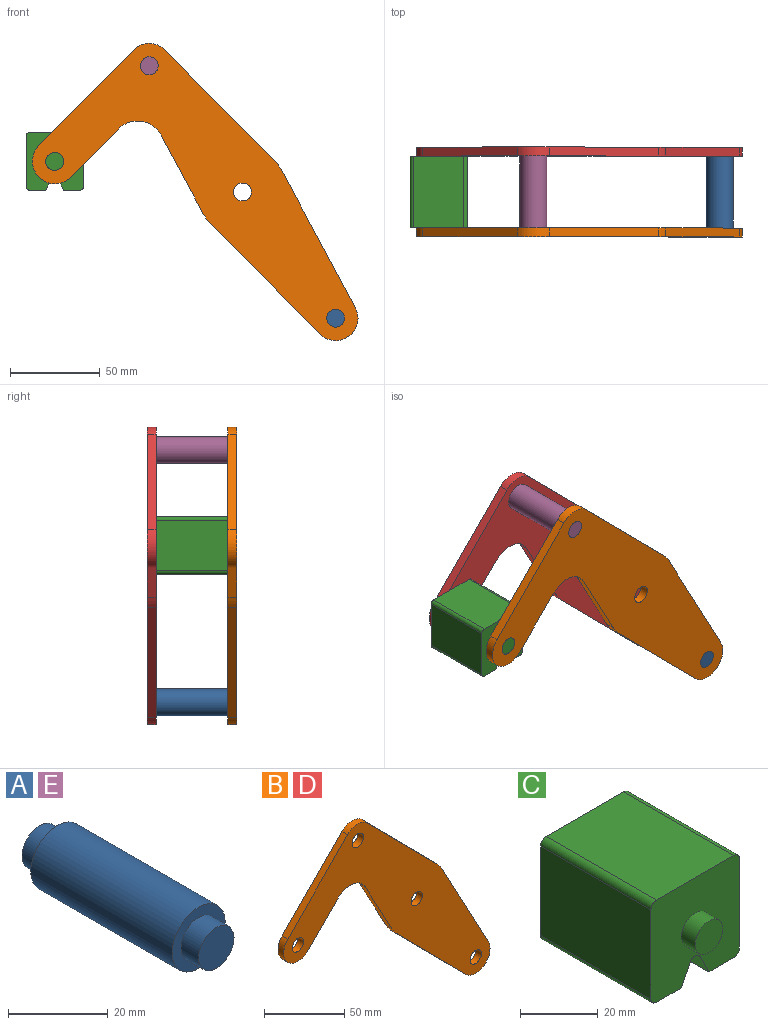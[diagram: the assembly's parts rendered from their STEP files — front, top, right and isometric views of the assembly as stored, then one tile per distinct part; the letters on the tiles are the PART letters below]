
ASSEMBLY  parts=5 mates=3
PART A: 7 faces, bbox 15x50x15 mm
  f0: cylinder r=7.5mm len=40mm, axis (0,-1,0), area 1885mm2, adj f2,f5
  f1: cylinder r=5mm len=10mm, axis (0,1,0), area 157.1mm2, adj f2,f3
  f2: plane 15x15mm, normal (0,-1,0), area 98.2mm2, adj f0,f1
  f3: plane 10x10mm, normal (0,-1,0), area 78.5mm2, adj f1
  f4: cylinder r=5mm len=10mm, axis (0,-1,0), area 157.1mm2, adj f5,f6
  f5: plane 15x15mm, normal (0,1,0), area 98.2mm2, adj f0,f4
  f6: plane 10x10mm, normal (0,1,0), area 78.5mm2, adj f4
PART B: 18 faces, bbox 181.7x5x165.8 mm
  f0: plane 43.49x23.35mm, normal (-0.88,0,-0.47), area 246.8mm2, adj f1,f14,f16,f17
  f1: cylinder r=25mm len=5.75mm, axis (0,1,0), area 35.8mm2, adj f0,f2,f16,f17
  f2: plane 61.6x60.87mm, normal (-0.71,0,-0.7), area 433mm2, adj f1,f3,f16,f17
  f3: cylinder r=12.5mm len=21.39mm, axis (0,1,0), area 178.4mm2, adj f2,f4,f16,f17
  f4: plane 76.3x40.96mm, normal (0.88,0,0.47), area 433mm2, adj f3,f5,f16,f17
  f5: cylinder r=25mm len=5.75mm, axis (0,1,0), area 35.8mm2, adj f4,f6,f16,f17
  f6: plane 61.6x60.87mm, normal (0.71,0,0.7), area 433mm2, adj f5,f7,f16,f17
  f7: cylinder r=12.5mm len=17.78mm, axis (0,1,0), area 98.9mm2, adj f6,f8,f16,f17
  f8: plane 53.35x52.71mm, normal (-0.71,0,0.7), area 375mm2, adj f7,f9,f16,f17
  f9: cylinder r=12.5mm len=21.39mm, axis (0,1,0), area 196.3mm2, adj f8,f10,f16,f17
  f10: plane 26.86x26.54mm, normal (0.71,0,-0.7), area 188.8mm2, adj f9,f14,f16,f17
  f11: cylinder r=5mm len=10mm, axis (0,1,0), area 157.1mm2, adj f16,f17
  f12: cylinder r=5mm len=10mm, axis (0,1,0), area 157.1mm2, adj f16,f17
  f13: cylinder r=5mm len=10mm, axis (0,1,0), area 157.1mm2, adj f16,f17
  f14: cylinder r=15mm len=23.89mm, axis (0,1,0), area 140.2mm2, adj f0,f10,f16,f17
  f15: cylinder r=5mm len=10mm, axis (0,1,0), area 157.1mm2, adj f16,f17
  f16: plane 181.66x165.78mm, normal (0,-1,0), area 8710.1mm2, adj f0,f1,f2,f3,f4,f5,f6,f7
  f17: plane 181.66x165.78mm, normal (0,1,0), area 8710.1mm2, adj f0,f1,f2,f3,f4,f5,f6,f7
PART C: 18 faces, bbox 32.1x50x32.1 mm
  f0: plane 40x28.08mm, normal (1,0,0), area 1123.1mm2, adj f4,f10,f13,f14
  f1: plane 40x9.04mm, normal (0,0,-1), area 361.6mm2, adj f2,f4,f10,f14
  f2: plane 40x6.42mm, normal (-0.89,0,-0.45), area 287.2mm2, adj f1,f4,f10,f15
  f3: plane 40x6.42mm, normal (0.89,0,-0.45), area 287.2mm2, adj f4,f5,f10,f15
  f4: plane 32.08x32.08mm, normal (0,-1,0), area 900.6mm2, adj f0,f1,f2,f3,f5,f6,f7,f9
  f5: plane 40x9.04mm, normal (0,0,-1), area 361.6mm2, adj f3,f4,f10,f16
  f6: plane 40x28.08mm, normal (0,0,1), area 1123.1mm2, adj f4,f10,f13,f17
  f7: plane 40x28.08mm, normal (-1,0,0), area 1123.1mm2, adj f4,f10,f16,f17
  f8: plane 10x10mm, normal (0,-1,0), area 78.5mm2, adj f9
  f9: cylinder r=5mm len=10mm, axis (0,1,0), area 157.1mm2, adj f4,f8
  f10: plane 32.08x32.08mm, normal (0,1,0), area 900.6mm2, adj f0,f1,f2,f3,f5,f6,f7,f12
  f11: plane 10x10mm, normal (0,1,0), area 78.5mm2, adj f12
  f12: cylinder r=5mm len=10mm, axis (0,-1,0), area 157.1mm2, adj f10,f11
  f13: cylinder r=2mm len=40mm, axis (0,1,0), area 125.7mm2, adj f0,f4,f6,f10
  f14: cylinder r=2mm len=40mm, axis (0,-1,0), area 125.7mm2, adj f0,f1,f4,f10
  f15: cylinder r=2mm len=40mm, axis (0,1,0), area 177.1mm2, adj f2,f3,f4,f10
  f16: cylinder r=2mm len=40mm, axis (0,1,0), area 125.7mm2, adj f4,f5,f7,f10
  f17: cylinder r=2mm len=40mm, axis (0,-1,0), area 125.7mm2, adj f4,f6,f7,f10
PART D: same geometry as B
PART E: same geometry as A
PLACE A t=(103.95,0,-140.78)mm
PLACE B at identity fixed
PLACE C at identity
PLACE D t=(0,45,0)mm
PLACE E at identity
MATE revolute B.f9 <-> C.f9  axis (0,1,0) through (-104.69,0,17.04)mm
MATE fastened E.f0 <-> D.f7  axis (0,1,0) through (-51.98,40,70.39)mm
MATE fastened A.f0 <-> B.f3  axis (0,-1,0) through (51.98,0,-70.39)mm
